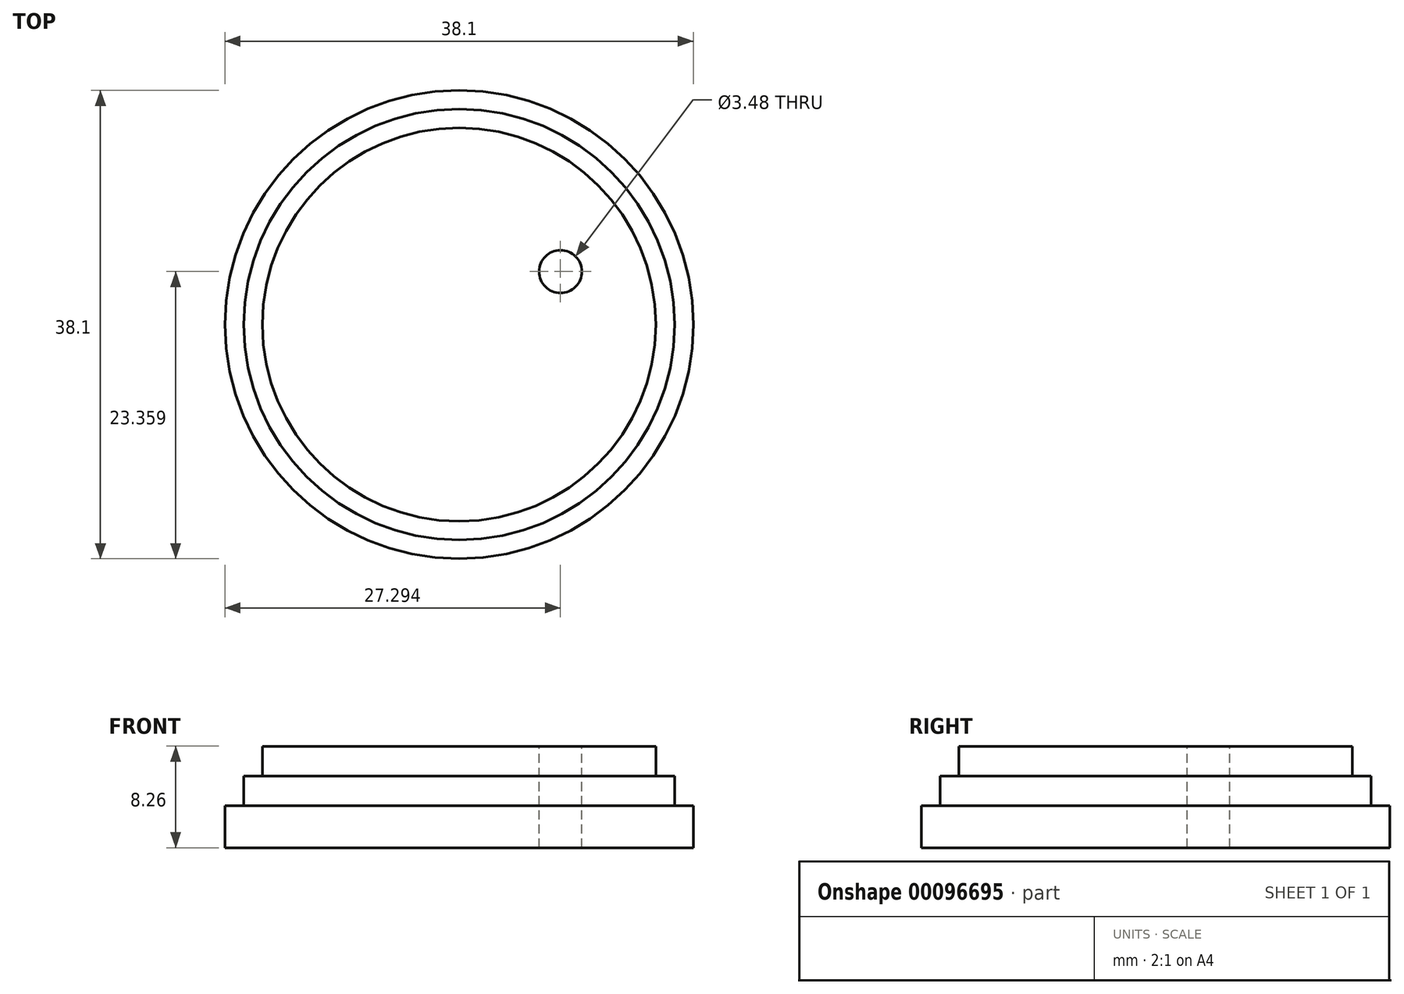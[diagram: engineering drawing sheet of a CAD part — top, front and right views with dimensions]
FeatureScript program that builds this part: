
annotation { "Feature Type Name" : "Feature", "Feature Type Description" : "" }
export const myFeature = defineFeature(function(context is Context, id is Id, definition is map)
    precondition{}
    {
        {
            var Q0;
            Q0=qCreatedBy(makeId("Front.planeOp"),FACE);
            var sketch = newSketch(context, id + "F0", { "sketchPlane" : qUnion([Q0])});
            skLineSegment(sketch, "E0", {"start": v(0, 0) * mm, "end": v(0, 3.43) * mm});
            skLineSegment(sketch, "E1", {"start": v(0, 3.43) * mm, "end": v(19.05, 3.43) * mm});
            skLineSegment(sketch, "E2", {"start": v(19.05, 3.43) * mm, "end": v(19.05, 0) * mm});
            skLineSegment(sketch, "E3", {"start": v(19.05, 0) * mm, "end": v(0, 0) * mm});
            skSolve(sketch);
        }
        {
            var Q0;
            Q0 = qSketchRegion(id + "F0", true);
            var Q1;
            Q1=sQuery(id+"F0.wireOp",EDGE,"E0");
            revolve(context, id + "F1", {"entities" : qUnion([Q0]), "axis" : qUnion([Q1]), "revolveType" : RevolveType.FULL});
        }
        {
            var Q0;
            Q0=qCreatedBy(makeId("Front.planeOp"),FACE);
            var sketch = newSketch(context, id + "F2", { "sketchPlane" : qUnion([Q0])});
            skLineSegment(sketch, "E4.bottom", {"start": v(0, 3.43) * mm, "end": v(17.53, 3.43) * mm});
            skLineSegment(sketch, "E4.top", {"start": v(0, 5.84) * mm, "end": v(17.53, 5.84) * mm});
            skLineSegment(sketch, "E4.left", {"start": v(0, 3.43) * mm, "end": v(0, 5.84) * mm});
            skLineSegment(sketch, "E4.right", {"start": v(17.53, 3.43) * mm, "end": v(17.53, 5.84) * mm});
            skSolve(sketch);
        }
        {
            var Q0;
            Q0 = qSketchRegion(id + "F2", true);
            var Q1;
            Q1=sQuery(id+"F2.wireOp",EDGE,"E4.left");
            revolve(context, id + "F3", {"operationType" : NewBodyOperationType.ADD, "entities" : qUnion([Q0]), "axis" : qUnion([Q1]), "revolveType" : RevolveType.FULL});
        }
        {
            var Q0;
            Q0=qCreatedBy(makeId("Front.planeOp"),FACE);
            var sketch = newSketch(context, id + "F4", { "sketchPlane" : qUnion([Q0])});
            skLineSegment(sketch, "E5.bottom", {"start": v(0, 5.84) * mm, "end": v(16, 5.84) * mm});
            skLineSegment(sketch, "E5.top", {"start": v(0, 8.25) * mm, "end": v(16, 8.25) * mm});
            skLineSegment(sketch, "E5.left", {"start": v(0, 5.84) * mm, "end": v(0, 8.25) * mm});
            skLineSegment(sketch, "E5.right", {"start": v(16, 5.84) * mm, "end": v(16, 8.25) * mm});
            skSolve(sketch);
        }
        {
            var Q0;
            Q0 = qSketchRegion(id + "F4", true);
            var Q1;
            Q1=sQuery(id+"F4.wireOp",EDGE,"E5.left");
            revolve(context, id + "F5", {"operationType" : NewBodyOperationType.ADD, "entities" : qUnion([Q0]), "axis" : qUnion([Q1]), "revolveType" : RevolveType.FULL});
        }
        {
            var Q0;
            Q0=makeQuery(id+"F5.opRevolve","SWEPT_FACE",FACE,{"disambiguationData":[OSD([sQuery(id+"F4.wireOp",EDGE,"E5.top")])]});
            var sketch = newSketch(context, id + "F6", { "sketchPlane" : qUnion([Q0])});
            skCircle(sketch, "E6", {"center": v(8.24, 4.3) * mm, "radius": 1.74 * mm});
            skSolve(sketch);
        }
        {
            var Q0;
            Q0 = qSketchRegion(id + "F6", true);
            extrude(context, id + "F7", {"entities" : qUnion([Q0]), "operationType" : NewBodyOperationType.REMOVE, "endBound" : BoundingType.THROUGH_ALL, "oppositeDirection" : true, "depth" : 8.35 * mm});
        }
    });
